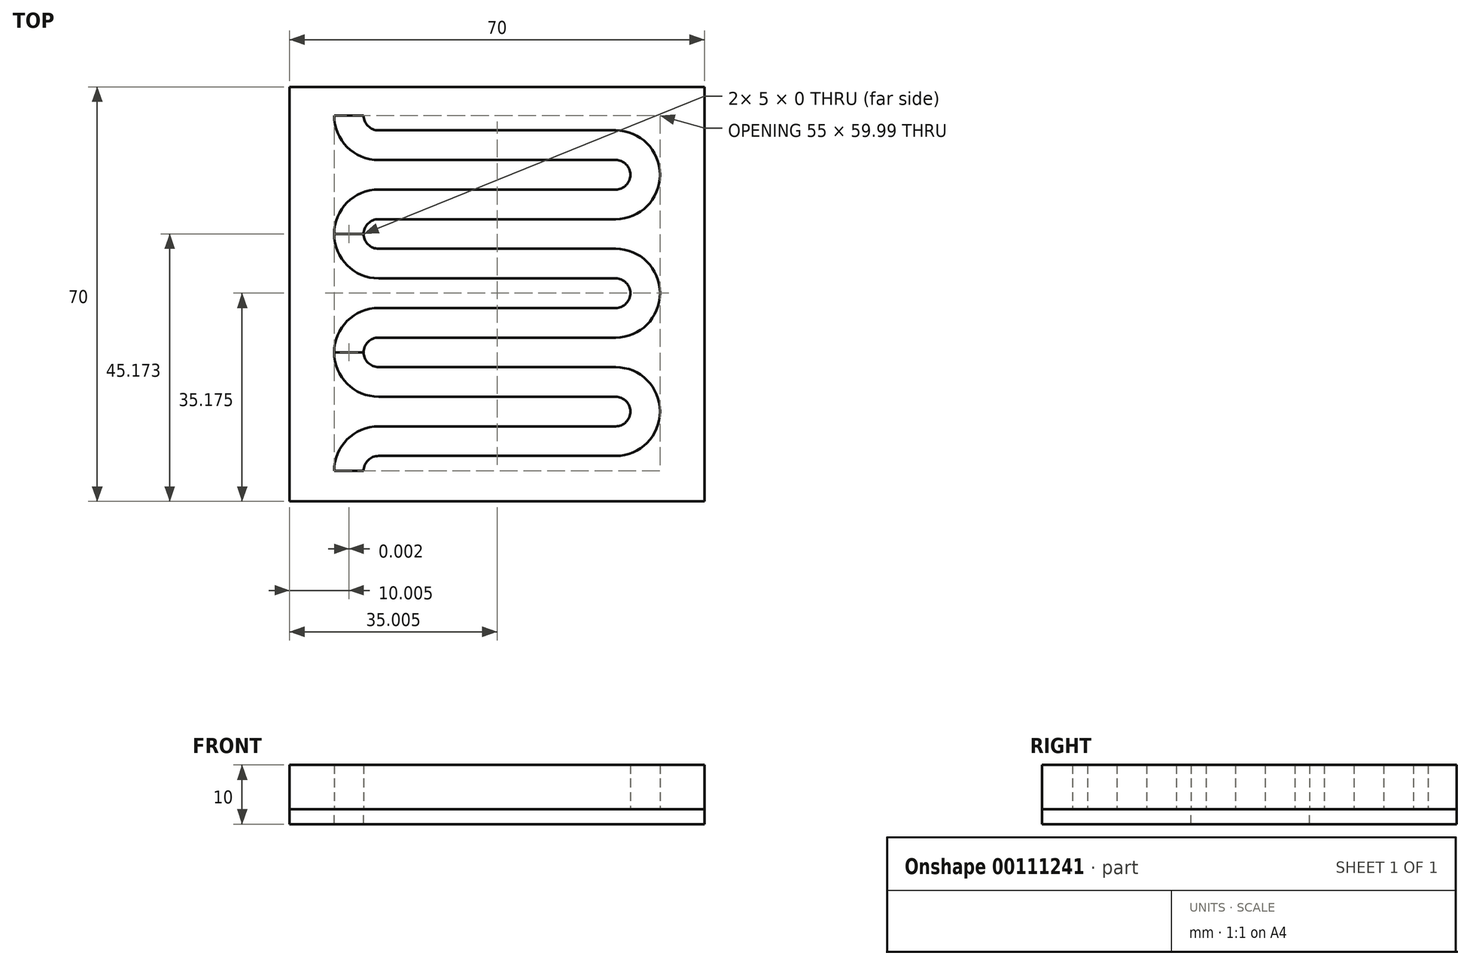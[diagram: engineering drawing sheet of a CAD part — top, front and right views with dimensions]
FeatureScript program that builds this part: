
annotation { "Feature Type Name" : "Feature", "Feature Type Description" : "" }
export const myFeature = defineFeature(function(context is Context, id is Id, definition is map)
    precondition{}
    {
        {
            var Q0;
            Q0=qCreatedBy(makeId("Top.planeOp"),FACE);
            var sketch = newSketch(context, id + "F0", { "sketchPlane" : qUnion([Q0])});
            skLineSegment(sketch, "E0", {"start": v(-23.37, 50.9) * mm, "end": v(-18.37, 50.9) * mm});
            skLineSegment(sketch, "E1", {"start": v(-18.37, 50.9) * mm, "end": v(-18.37, 50.9) * mm});
            skLineSegment(sketch, "E2", {"start": v(-15.87, 48.4) * mm, "end": v(24.13, 48.4) * mm});
            skLineSegment(sketch, "E3", {"start": v(31.63, 40.9) * mm, "end": v(31.63, 40.9) * mm});
            skLineSegment(sketch, "E4", {"start": v(24.13, 33.4) * mm, "end": v(-15.87, 33.4) * mm});
            skLineSegment(sketch, "E5", {"start": v(-18.37, 30.9) * mm, "end": v(-18.37, 30.9) * mm});
            skLineSegment(sketch, "E6", {"start": v(-18.37, 30.9) * mm, "end": v(-23.37, 30.9) * mm});
            skLineSegment(sketch, "E7", {"start": v(-23.37, 30.9) * mm, "end": v(-23.37, 30.9) * mm});
            skLineSegment(sketch, "E8", {"start": v(-15.87, 38.4) * mm, "end": v(24.13, 38.4) * mm});
            skLineSegment(sketch, "E9", {"start": v(26.63, 40.9) * mm, "end": v(26.63, 40.9) * mm});
            skLineSegment(sketch, "E10", {"start": v(24.13, 43.4) * mm, "end": v(-15.87, 43.4) * mm});
            skLineSegment(sketch, "E11", {"start": v(-23.37, 50.9) * mm, "end": v(-23.37, 50.9) * mm});
            skArc(sketch, "E12.filletArc", {"start": v(31.63, 40.9) * mm, "mid": v(29.43, 46.21) * mm, "end": v(24.13, 48.4) * mm});
            skArc(sketch, "E13.filletArc", {"start": v(24.13, 33.4) * mm, "mid": v(29.43, 35.6) * mm, "end": v(31.63, 40.9) * mm});
            skArc(sketch, "E14.filletArc", {"start": v(26.63, 40.9) * mm, "mid": v(25.9, 42.68) * mm, "end": v(24.13, 43.4) * mm});
            skArc(sketch, "E15.filletArc", {"start": v(24.13, 38.4) * mm, "mid": v(25.9, 39.14) * mm, "end": v(26.63, 40.9) * mm});
            skArc(sketch, "E16.filletArc", {"start": v(-18.37, 50.9) * mm, "mid": v(-17.64, 49.14) * mm, "end": v(-15.87, 48.4) * mm});
            skArc(sketch, "E17.filletArc", {"start": v(-23.37, 50.9) * mm, "mid": v(-21.18, 45.6) * mm, "end": v(-15.87, 43.4) * mm});
            skArc(sketch, "E18.filletArc", {"start": v(-15.87, 38.4) * mm, "mid": v(-21.18, 36.21) * mm, "end": v(-23.37, 30.9) * mm});
            skArc(sketch, "E19.filletArc", {"start": v(-15.87, 33.4) * mm, "mid": v(-17.64, 32.68) * mm, "end": v(-18.37, 30.9) * mm});
            skLineSegment(sketch, "E20.0.1.3", {"start": v(-15.87, 58.4) * mm, "end": v(24.13, 58.4) * mm});
            skLineSegment(sketch, "E20.0.1.4", {"start": v(24.13, 63.4) * mm, "end": v(-15.87, 63.4) * mm});
            skLineSegment(sketch, "E20.0.1.6", {"start": v(-15.87, 68.4) * mm, "end": v(24.13, 68.4) * mm});
            skLineSegment(sketch, "E20.0.1.7", {"start": v(-18.37, 50.9) * mm, "end": v(-23.37, 50.9) * mm});
            skLineSegment(sketch, "E20.0.1.8", {"start": v(24.13, 53.4) * mm, "end": v(-15.87, 53.4) * mm});
            skArc(sketch, "E20.0.1.10", {"start": v(-15.87, 58.4) * mm, "mid": v(-21.18, 56.2) * mm, "end": v(-23.37, 50.9) * mm});
            skArc(sketch, "E20.0.1.13", {"start": v(31.63, 60.9) * mm, "mid": v(29.43, 66.2) * mm, "end": v(24.13, 68.4) * mm});
            skArc(sketch, "E20.0.1.14", {"start": v(24.13, 53.4) * mm, "mid": v(29.43, 55.6) * mm, "end": v(31.63, 60.9) * mm});
            skLineSegment(sketch, "E20.0.1.15", {"start": v(-23.37, 70.9) * mm, "end": v(-18.37, 70.9) * mm});
            skArc(sketch, "E20.0.1.17", {"start": v(-23.37, 70.9) * mm, "mid": v(-21.18, 65.6) * mm, "end": v(-15.87, 63.4) * mm});
            skArc(sketch, "E20.0.1.18", {"start": v(24.13, 58.4) * mm, "mid": v(25.9, 59.14) * mm, "end": v(26.63, 60.9) * mm});
            skArc(sketch, "E20.0.1.19", {"start": v(-18.37, 70.9) * mm, "mid": v(-17.64, 69.14) * mm, "end": v(-15.87, 68.4) * mm});
            skArc(sketch, "E20.0.1.20", {"start": v(26.63, 60.9) * mm, "mid": v(25.9, 62.67) * mm, "end": v(24.13, 63.4) * mm});
            skArc(sketch, "E20.0.1.21", {"start": v(-15.87, 53.4) * mm, "mid": v(-17.64, 52.67) * mm, "end": v(-18.37, 50.9) * mm});
            skLineSegment(sketch, "E20.0.2.3", {"start": v(-15.88, 78.4) * mm, "end": v(24.12, 78.4) * mm});
            skLineSegment(sketch, "E20.0.2.4", {"start": v(24.12, 83.4) * mm, "end": v(-15.88, 83.4) * mm});
            skLineSegment(sketch, "E20.0.2.6", {"start": v(-15.88, 88.4) * mm, "end": v(24.12, 88.4) * mm});
            skLineSegment(sketch, "E20.0.2.7", {"start": v(-18.38, 70.9) * mm, "end": v(-23.38, 70.9) * mm});
            skLineSegment(sketch, "E20.0.2.8", {"start": v(24.12, 73.4) * mm, "end": v(-15.88, 73.4) * mm});
            skArc(sketch, "E20.0.2.10", {"start": v(-15.88, 78.4) * mm, "mid": v(-21.18, 76.2) * mm, "end": v(-23.38, 70.9) * mm});
            skArc(sketch, "E20.0.2.13", {"start": v(31.62, 80.9) * mm, "mid": v(29.43, 86.2) * mm, "end": v(24.12, 88.4) * mm});
            skArc(sketch, "E20.0.2.14", {"start": v(24.12, 73.4) * mm, "mid": v(29.43, 75.6) * mm, "end": v(31.62, 80.9) * mm});
            skLineSegment(sketch, "E20.0.2.15", {"start": v(-23.38, 90.9) * mm, "end": v(-18.38, 90.9) * mm});
            skArc(sketch, "E20.0.2.17", {"start": v(-23.38, 90.9) * mm, "mid": v(-21.18, 85.6) * mm, "end": v(-15.88, 83.4) * mm});
            skArc(sketch, "E20.0.2.18", {"start": v(24.12, 78.4) * mm, "mid": v(25.9, 79.13) * mm, "end": v(26.62, 80.9) * mm});
            skArc(sketch, "E20.0.2.19", {"start": v(-18.38, 90.9) * mm, "mid": v(-17.64, 89.13) * mm, "end": v(-15.88, 88.4) * mm});
            skArc(sketch, "E20.0.2.20", {"start": v(26.62, 80.9) * mm, "mid": v(25.9, 82.67) * mm, "end": v(24.12, 83.4) * mm});
            skArc(sketch, "E20.0.2.21", {"start": v(-15.88, 73.4) * mm, "mid": v(-17.64, 72.67) * mm, "end": v(-18.38, 70.9) * mm});
            skLineSegment(sketch, "E20.direction1", {"start": v(-23.37, 30.9) * mm, "end": v(2.03, 30.9) * mm, "construction": true});
            skLineSegment(sketch, "E20.direction2", {"start": v(-23.37, 30.9) * mm, "end": v(-23.37, 50.9) * mm, "construction": true});
            skLineSegment(sketch, "E21.bottom", {"start": v(-30.88, 95.73) * mm, "end": v(39.12, 95.73) * mm});
            skLineSegment(sketch, "E21.top", {"start": v(-30.88, 25.73) * mm, "end": v(39.12, 25.73) * mm});
            skLineSegment(sketch, "E21.left", {"start": v(-30.88, 95.73) * mm, "end": v(-30.88, 25.73) * mm});
            skLineSegment(sketch, "E21.right", {"start": v(39.12, 95.73) * mm, "end": v(39.12, 25.73) * mm});
            skLineSegment(sketch, "E22", {"start": v(-23.38, 90.9) * mm, "end": v(-23.38, 95.73) * mm});
            skLineSegment(sketch, "E23", {"start": v(-18.38, 90.9) * mm, "end": v(-18.38, 95.73) * mm});
            skLineSegment(sketch, "E24", {"start": v(-23.37, 30.9) * mm, "end": v(-23.37, 25.73) * mm});
            skLineSegment(sketch, "E25", {"start": v(-18.37, 30.9) * mm, "end": v(-18.37, 25.73) * mm});
            skPoint(sketch, "E26", {"position": v(-20.87, 25.73) * mm});
            skPoint(sketch, "E27", {"position": v(-20.9, 95.73) * mm});
            skSolve(sketch);
        }
        {
            var Q0;
            Q0=makeQuery(id+"F0.imprint","IMPRINT",FACE,{"disambiguationData":[TD([[makeQuery(id+"F0.imprint","IMPRINT",EDGE,{"derivedFrom":sQuery(id+"F0.wireOp",EDGE,"E8")}),1.0]])]});
            var Q1;
            Q1=makeQuery(id+"F0.imprint","IMPRINT",FACE,{"disambiguationData":[TD([[makeQuery(id+"F0.imprint","IMPRINT",EDGE,{"derivedFrom":sQuery(id+"F0.wireOp",EDGE,"E2")}),1.0]])]});
            var Q2;
            Q2=makeQuery(id+"F0.imprint","IMPRINT",FACE,{"disambiguationData":[TD([[makeQuery(id+"F0.imprint","IMPRINT",EDGE,{"derivedFrom":sQuery(id+"F0.wireOp",EDGE,"E20.0.2.15")}),1.0]])]});
            var Q3;
            Q3=makeQuery(id+"F0.imprint","IMPRINT",FACE,{"disambiguationData":[TD([[makeQuery(id+"F0.imprint","IMPRINT",EDGE,{"derivedFrom":sQuery(id+"F0.wireOp",EDGE,"E6")}),1.0]])]});
            extrude(context, id + "F1", {"entities" : qUnion([Q0, Q1, Q2, Q3]), "depth" : 7.5 * mm});
        }
        {
            var Q0;
            Q0=makeQuery(id+"F0.imprint","IMPRINT",FACE,{"disambiguationData":[TD([[makeQuery(id+"F0.imprint","IMPRINT",EDGE,{"derivedFrom":sQuery(id+"F0.wireOp",EDGE,"E20.0.1.3")}),-1.0]])]});
            var Q1;
            Q1=makeQuery(id+"F0.imprint","IMPRINT",FACE,{"disambiguationData":[TD([[makeQuery(id+"F0.imprint","IMPRINT",EDGE,{"derivedFrom":sQuery(id+"F0.wireOp",EDGE,"E2")}),-1.0]])]});
            var Q2;
            Q2=makeQuery(id+"F0.imprint","IMPRINT",FACE,{"disambiguationData":[TD([[makeQuery(id+"F0.imprint","IMPRINT",EDGE,{"derivedFrom":sQuery(id+"F0.wireOp",EDGE,"E20.0.2.15")}),1.0]])]});
            var Q3;
            Q3=makeQuery(id+"F0.imprint","IMPRINT",FACE,{"disambiguationData":[TD([[makeQuery(id+"F0.imprint","IMPRINT",EDGE,{"derivedFrom":sQuery(id+"F0.wireOp",EDGE,"E6")}),1.0]])]});
            var Q4;
            Q4=makeQuery(id+"F0.imprint","IMPRINT",FACE,{"disambiguationData":[TD([[makeQuery(id+"F0.imprint","IMPRINT",EDGE,{"derivedFrom":sQuery(id+"F0.wireOp",EDGE,"E8")}),1.0]])]});
            var Q5;
            Q5=makeQuery(id+"F0.imprint","IMPRINT",FACE,{"disambiguationData":[TD([[makeQuery(id+"F0.imprint","IMPRINT",EDGE,{"derivedFrom":sQuery(id+"F0.wireOp",EDGE,"E20.0.2.3")}),-1.0]])]});
            var Q6;
            Q6=makeQuery(id+"F0.imprint","IMPRINT",FACE,{"disambiguationData":[TD([[makeQuery(id+"F0.imprint","IMPRINT",EDGE,{"derivedFrom":sQuery(id+"F0.wireOp",EDGE,"E2")}),1.0]])]});
            extrude(context, id + "F2", {"entities" : qUnion([Q0, Q1, Q2, Q3, Q4, Q5, Q6]), "oppositeDirection" : true, "depth" : 2.5 * mm});
        }
    });
